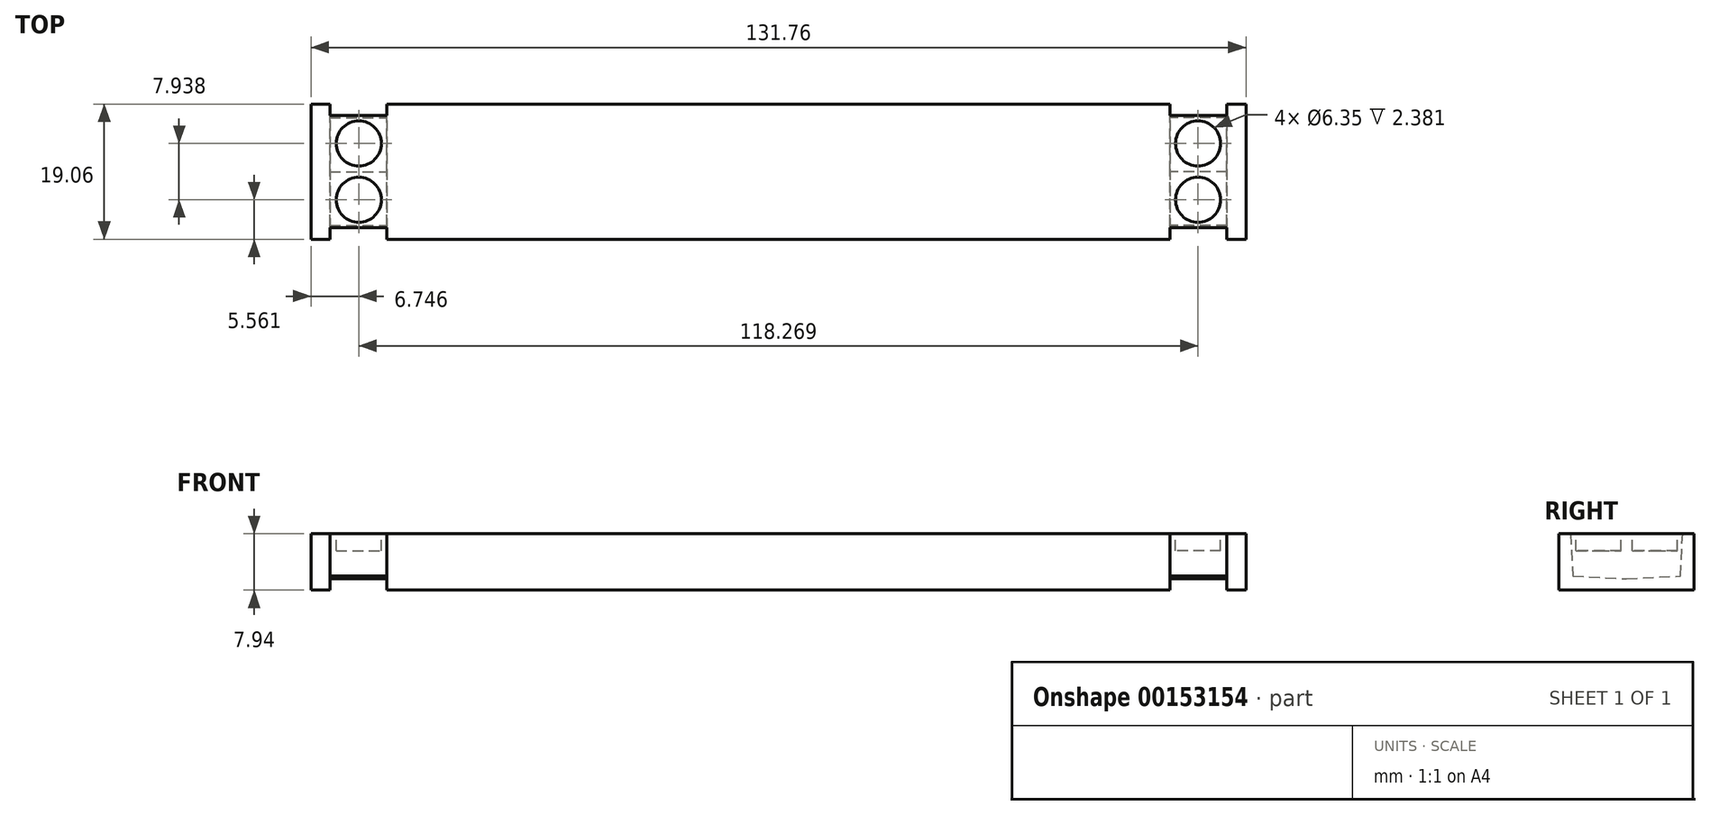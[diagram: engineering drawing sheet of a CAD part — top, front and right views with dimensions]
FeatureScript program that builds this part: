
annotation { "Feature Type Name" : "Feature", "Feature Type Description" : "" }
export const myFeature = defineFeature(function(context is Context, id is Id, definition is map)
    precondition{}
    {
        {
            var Q0;
            Q0=qCreatedBy(makeId("Top.planeOp"),FACE);
            var sketch = newSketch(context, id + "F0", { "sketchPlane" : qUnion([Q0])});
            skLineSegment(sketch, "E0.bottom", {"start": v(65.88, -9.52) * mm, "end": v(63.2, -9.52) * mm});
            skLineSegment(sketch, "E0.top", {"start": v(65.88, 9.53) * mm, "end": v(63.2, 9.53) * mm});
            skLineSegment(sketch, "E0.left", {"start": v(65.88, -9.52) * mm, "end": v(65.88, 9.53) * mm});
            skPoint(sketch, "E0.middle", {"position": v(0, 0) * mm});
            skLineSegment(sketch, "E1.top", {"start": v(55.17, 7.89) * mm, "end": v(63.2, 7.89) * mm});
            skLineSegment(sketch, "E1.left", {"start": v(55.17, 9.53) * mm, "end": v(55.17, 7.89) * mm});
            skLineSegment(sketch, "E1.right", {"start": v(63.2, 9.53) * mm, "end": v(63.2, 7.89) * mm});
            skLineSegment(sketch, "E2.trimOffspring", {"start": v(55.17, 9.53) * mm, "end": v(0, 9.53) * mm});
            skLineSegment(sketch, "E3", {"start": v(-71.66, 0) * mm, "end": v(70.2, 0) * mm, "construction": true});
            skLineSegment(sketch, "E4.MirrorCS", {"start": v(55.17, -7.89) * mm, "end": v(63.2, -7.89) * mm});
            skLineSegment(sketch, "E5.MirrorCS", {"start": v(63.2, -9.53) * mm, "end": v(63.2, -7.89) * mm});
            skLineSegment(sketch, "E6.MirrorCS", {"start": v(55.17, -9.53) * mm, "end": v(55.17, -7.89) * mm});
            skLineSegment(sketch, "E7.trimOffspring", {"start": v(55.17, -9.52) * mm, "end": v(0, -9.53) * mm});
            skLineSegment(sketch, "E8", {"start": v(0, 9.52) * mm, "end": v(0, -9.52) * mm});
            skSolve(sketch);
        }
        {
            var Q0;
            Q0=qSketchRegion(id+"F0",true);
            extrude(context, id + "F1", {"entities" : qUnion([Q0]), "oppositeDirection" : true, "depth" : 7.94 * mm});
        }
        {
            var Q0;
            Q0=makeQuery(id+"F1.opExtrude","CAP_FACE",FACE,{"disambiguationData":[OSD([sQuery(id+"F0.wireOp",EDGE,"E0.bottom"),sQuery(id+"F0.wireOp",EDGE,"E0.top"),sQuery(id+"F0.wireOp",EDGE,"E0.left"),sQuery(id+"F0.wireOp",EDGE,"E0.right"),sQuery(id+"F0.wireOp",EDGE,"E1.top"),sQuery(id+"F0.wireOp",EDGE,"E1.left"),sQuery(id+"F0.wireOp",EDGE,"E1.right"),sQuery(id+"F0.wireOp",EDGE,"n9GokV4e-7PqV-T5PN-pgQq-kAGkPthqguKu.top"),sQuery(id+"F0.wireOp",EDGE,"n9GokV4e-7PqV-T5PN-pgQq-kAGkPthqguKu.left"),sQuery(id+"F0.wireOp",EDGE,"n9GokV4e-7PqV-T5PN-pgQq-kAGkPthqguKu.right"),sQuery(id+"F0.wireOp",EDGE,"E2.trimOffspring"),sQuery(id+"F0.wireOp",EDGE,"8a878713-a94b-462d-b4c5-ed988c78c997.trimOffspring"),sQuery(id+"F0.wireOp",EDGE,"468df20e-3106-4994-8e24-3c26fe30d41d0.MirrorCS"),sQuery(id+"F0.wireOp",EDGE,"468df20e-3106-4994-8e24-3c26fe30d41d1.MirrorCS"),sQuery(id+"F0.wireOp",EDGE,"468df20e-3106-4994-8e24-3c26fe30d41d2.MirrorCS"),sQuery(id+"F0.wireOp",EDGE,"E4.MirrorCS"),sQuery(id+"F0.wireOp",EDGE,"E5.MirrorCS"),sQuery(id+"F0.wireOp",EDGE,"E6.MirrorCS"),sQuery(id+"F0.wireOp",EDGE,"c9c867c6-7724-400b-9de4-c7a81ab06d04.trimOffspring"),sQuery(id+"F0.wireOp",EDGE,"E7.trimOffspring")])],"isStart":true});
            var sketch = newSketch(context, id + "F2", { "sketchPlane" : qUnion([Q0])});
            skCircle(sketch, "E9", {"center": v(59.13, 3.97) * mm, "radius": 3.18 * mm});
            skCircle(sketch, "E10", {"center": v(-59.13, 3.97) * mm, "radius": 3.18 * mm});
            skCircle(sketch, "E11.MirrorC", {"center": v(-59.13, -3.97) * mm, "radius": 3.18 * mm});
            skCircle(sketch, "E12.MirrorC", {"center": v(59.13, -3.97) * mm, "radius": 3.18 * mm});
            skSolve(sketch);
        }
        {
            var Q0;
            Q0=qSketchRegion(id+"F2",true);
            extrude(context, id + "F3", {"entities" : qUnion([Q0]), "operationType" : NewBodyOperationType.REMOVE, "oppositeDirection" : true, "depth" : 2.38 * mm});
        }
        {
            var Q0;
            Q0=makeQuery(id+"F1.opExtrude","SWEPT_FACE",FACE,{"disambiguationData":[OSD([sQuery(id+"F0.wireOp",EDGE,"E6.MirrorCS")])]});
            cPlane(context, id + "F4", {"entities" : qUnion([Q0]), "cplaneType" : CPlaneType.OFFSET, "offset" : 0 * mm, "width" : 152.4 * mm, "height" : 152.4 * mm});
        }
        {
            var Q0;
            Q0=qCreatedBy(id+"F4.planeOp",FACE);
            var sketch = newSketch(context, id + "F5", { "sketchPlane" : qUnion([Q0])});
            skLineSegment(sketch, "E13", {"start": v(-7.89, 0) * mm, "end": v(-7.57, -5.95) * mm});
            skLineSegment(sketch, "E14", {"start": v(-7.57, -5.95) * mm, "end": v(0, -6.35) * mm});
            skLineSegment(sketch, "E15", {"start": v(0, -6.35) * mm, "end": v(7.57, -5.95) * mm});
            skLineSegment(sketch, "E16", {"start": v(7.57, -5.95) * mm, "end": v(7.89, 0) * mm});
            skLineSegment(sketch, "E17", {"start": v(7.89, 0) * mm, "end": v(9.53, 0) * mm});
            skLineSegment(sketch, "E18", {"start": v(9.53, 0) * mm, "end": v(9.53, -7.94) * mm});
            skLineSegment(sketch, "E19", {"start": v(9.53, -7.94) * mm, "end": v(-9.52, -7.94) * mm});
            skLineSegment(sketch, "E20", {"start": v(-9.52, -7.94) * mm, "end": v(-9.52, 0) * mm});
            skLineSegment(sketch, "E21", {"start": v(-9.52, 0) * mm, "end": v(-7.89, 0) * mm});
            skLineSegment(sketch, "E22", {"start": v(-7.89, 0) * mm, "end": v(-7.89, -7.94) * mm, "construction": true});
            skLineSegment(sketch, "E23", {"start": v(7.89, 0) * mm, "end": v(7.89, -7.94) * mm, "construction": true});
            skSolve(sketch);
        }
        {
            var Q0;
            Q0=qSketchRegion(id+"F5",true);
            var Q1;
            Q1=makeQuery(id+"F1.opExtrude","SWEPT_FACE",FACE,{"disambiguationData":[OSD([sQuery(id+"F0.wireOp",EDGE,"E5.MirrorCS")])]});
            extrude(context, id + "F6", {"entities" : qUnion([Q0]), "operationType" : NewBodyOperationType.REMOVE, "endBound" : BoundingType.UP_TO_SURFACE, "endBoundEntityFace" : qUnion([Q1]), "depth" : 8.03 * mm});
        }
        {
            var Q0;
            Q0=makeQuery(id+"F1.opExtrude","SWEPT_BODY",BODY,{"disambiguationData":[OSD([sQuery(id+"F0.wireOp",EDGE,"E0.bottom"),sQuery(id+"F0.wireOp",EDGE,"E0.top"),sQuery(id+"F0.wireOp",EDGE,"E0.left"),sQuery(id+"F0.wireOp",EDGE,"E1.top"),sQuery(id+"F0.wireOp",EDGE,"E1.left"),sQuery(id+"F0.wireOp",EDGE,"E1.right"),sQuery(id+"F0.wireOp",EDGE,"E2.trimOffspring"),sQuery(id+"F0.wireOp",EDGE,"E4.MirrorCS"),sQuery(id+"F0.wireOp",EDGE,"E5.MirrorCS"),sQuery(id+"F0.wireOp",EDGE,"E6.MirrorCS"),sQuery(id+"F0.wireOp",EDGE,"E7.trimOffspring"),sQuery(id+"F0.wireOp",EDGE,"E8")])]});
            var Q1;
            Q1=qCreatedBy(makeId("Right.planeOp"),FACE);
            mirror(context, id + "F7", {"operationType" : NewBodyOperationType.ADD, "entities" : qUnion([Q0]), "mirrorPlane" : qUnion([Q1])});
        }
    });
